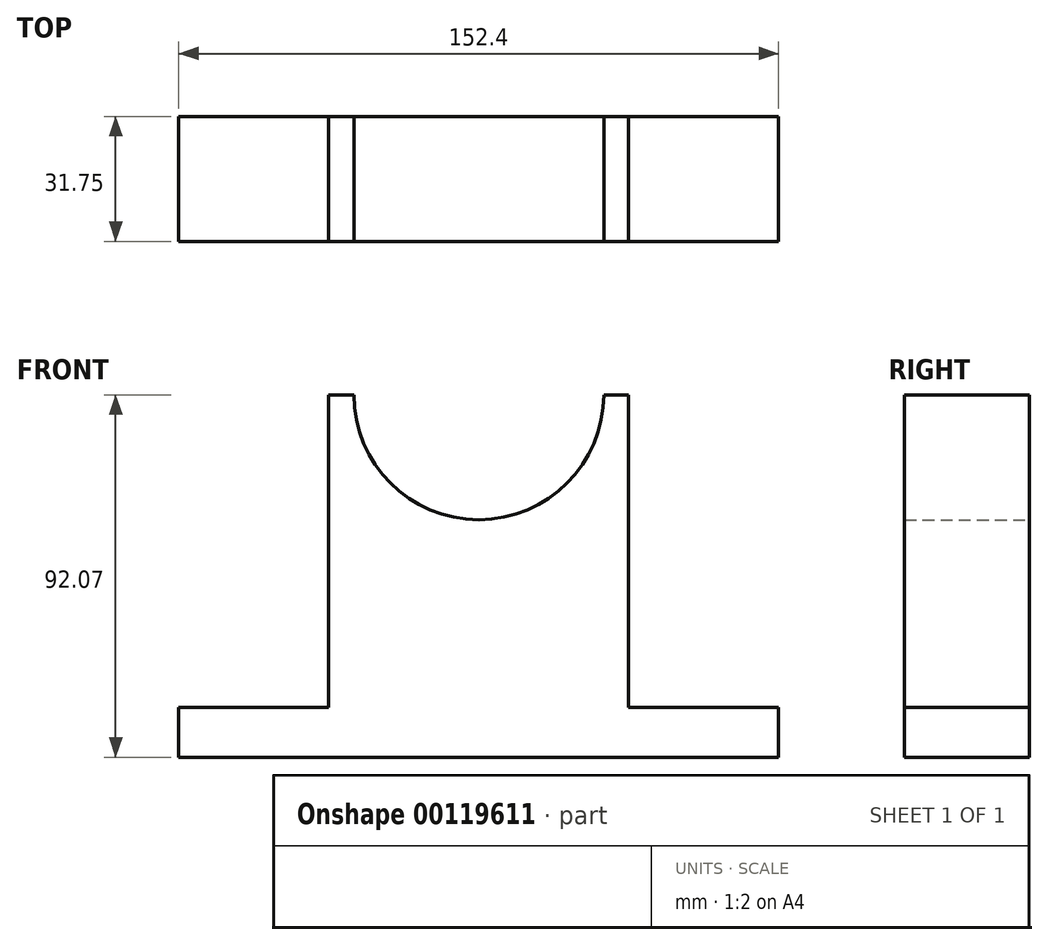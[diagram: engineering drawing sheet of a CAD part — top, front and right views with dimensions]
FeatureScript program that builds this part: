
annotation { "Feature Type Name" : "Feature", "Feature Type Description" : "" }
export const myFeature = defineFeature(function(context is Context, id is Id, definition is map)
    precondition{}
    {
        {
            var Q0;
            Q0=qCreatedBy(makeId("Front.planeOp"),FACE);
            var sketch = newSketch(context, id + "F0", { "sketchPlane" : qUnion([Q0])});
            skLineSegment(sketch, "E0", {"start": v(-76.23, -77.13) * mm, "end": v(-76.23, -64.43) * mm});
            skLineSegment(sketch, "E1", {"start": v(-76.23, -64.43) * mm, "end": v(-38.13, -64.43) * mm});
            skLineSegment(sketch, "E2", {"start": v(-38.13, -64.43) * mm, "end": v(-38.13, 14.94) * mm});
            skLineSegment(sketch, "E3", {"start": v(-38.13, 14.94) * mm, "end": v(38.07, 14.94) * mm});
            skLineSegment(sketch, "E4", {"start": v(38.07, 14.94) * mm, "end": v(38.07, -64.43) * mm});
            skLineSegment(sketch, "E5", {"start": v(38.07, -64.43) * mm, "end": v(76.17, -64.43) * mm});
            skLineSegment(sketch, "E6", {"start": v(76.17, -64.43) * mm, "end": v(76.17, -77.13) * mm});
            skLineSegment(sketch, "E7", {"start": v(76.17, -77.13) * mm, "end": v(-76.23, -77.13) * mm});
            skArc(sketch, "E8", {"start": v(-31.75, 14.94) * mm, "mid": v(0, -16.8) * mm, "end": v(31.75, 14.94) * mm});
            skSolve(sketch);
        }
        {
            var Q0;
            Q0=makeQuery(id+"F0.imprint","IMPRINT",FACE,{"disambiguationData":[TD([[makeQuery(id+"F0.imprint","IMPRINT",EDGE,{"derivedFrom":sQuery(id+"F0.wireOp",EDGE,"E0")}),-1.0]])]});
            extrude(context, id + "F1", {"entities" : qUnion([Q0]), "depth" : 31.75 * mm});
        }
    });
